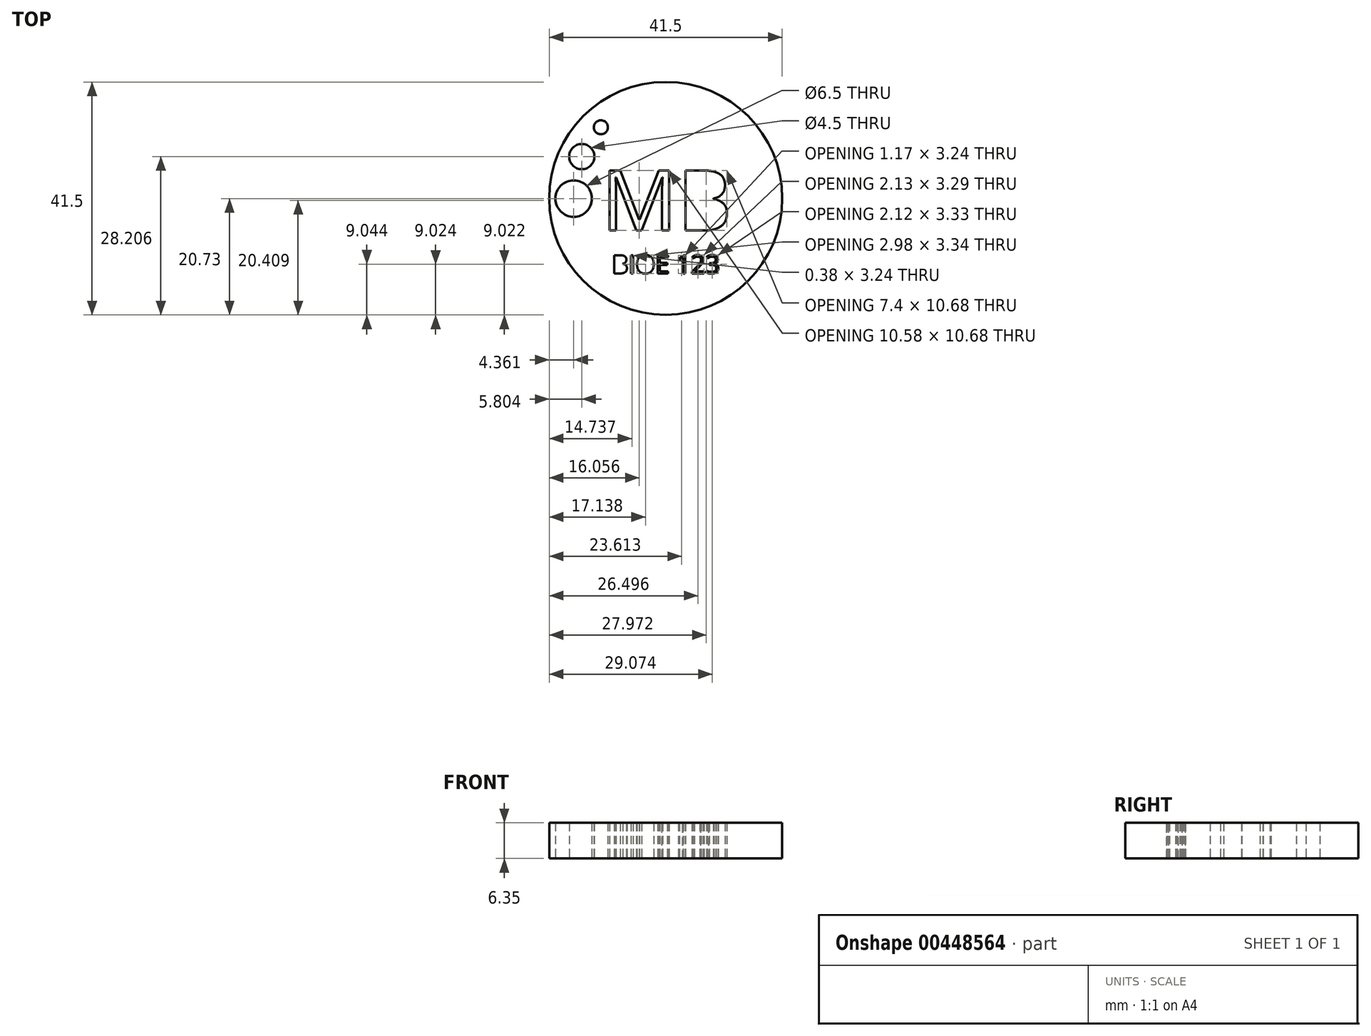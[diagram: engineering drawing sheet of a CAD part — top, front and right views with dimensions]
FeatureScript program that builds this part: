
annotation { "Feature Type Name" : "Feature", "Feature Type Description" : "" }
export const myFeature = defineFeature(function(context is Context, id is Id, definition is map)
    precondition{}
    {
        {
            var Q0;
            Q0=qCreatedBy(makeId("Top.planeOp"),FACE);
            var sketch = newSketch(context, id + "F0", { "sketchPlane" : qUnion([Q0])});
            skCircle(sketch, "E0", {"center": v(-0.05, 0.04) * mm, "radius": 20.75 * mm});
            skCircle(sketch, "E1", {"center": v(-11.6, 12.72) * mm, "radius": 1.25 * mm});
            skCircle(sketch, "E2", {"center": v(-15, 7.5) * mm, "radius": 2.25 * mm});
            skCircle(sketch, "E3", {"center": v(-16.44, 0.02) * mm, "radius": 3.25 * mm});
            skText(sketch, "E4", { "text": "MB", "fontName": "OpenSans-Regular.ttf"});
            skText(sketch, "E5", { "text": "BIOE 123", "fontName": "OpenSans-Regular.ttf"});
            const initialGuessF0  = {"E4": [-0.0115, -0.00564, 1, 0, 0.01077], "E5": [-0.00964, -0.01331, 1, 0, 0.00327]};
            skSetInitialGuess(sketch, initialGuessF0);
            skSolve(sketch);
        }
        {
            var Q0;
            Q0 = qSketchRegion(id + "F0", true);
            extrude(context, id + "F1", {"entities" : qUnion([Q0]), "depth" : 6.35 * mm});
        }
    });
